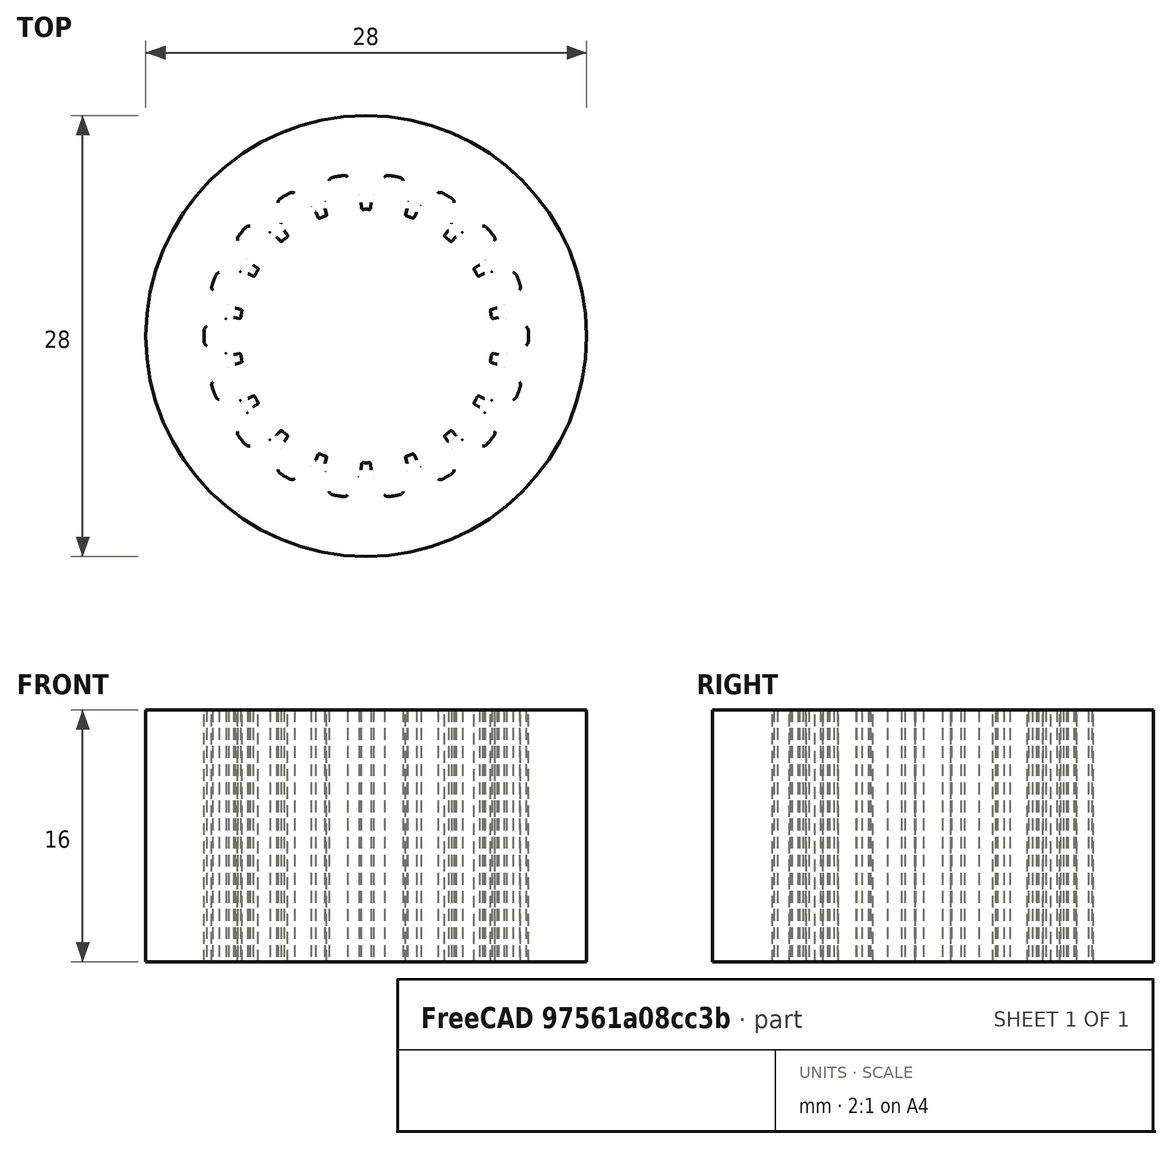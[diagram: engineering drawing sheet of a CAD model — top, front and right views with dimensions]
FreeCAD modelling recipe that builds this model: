
FCSTD DOCUMENT  (FreeCAD 0.19R24276 (Git))
Label: Gear_privod_perehodnik_to_GT2_gear_part_offset_3_d28_h16
License: All rights reserved
LicenseURL: http://en.wikipedia.org/wiki/All_rights_reserved
objects: Part::Part2DObjectPython×1, Part::Offset2D×1, Part::Cylinder×1, Part::Extrusion×1, Part::Cut×1
note: 5 computed .brp shape members not serialized (recipe doc carries the construction recipe); baked Part::Feature solids carry a one-line shape summary decoded from their .brp

FEATURE [Part::Part2DObjectPython] InvoluteGear  # Draft 2D object (typed FeaturePython)
  ExternalGear = true
  HighPrecision = true
  Modules = 1
  NumberOfTeeth = 18
  PressureAngle = 20
FEATURE [Part::Offset2D] Offset2D
  Fill = false
  Intersection = false
  Join = 0
  Mode = 1
  SelfIntersection = false
  Source = -> InvoluteGear
  Value = 0.3
FEATURE [Part::Cylinder] Cylinder  label="Цилиндр"
  Angle = 360
  AttacherType = Attacher::AttachEngine3D
  Height = 16
  Placement = pos=(0,0,-16) rot=(0,0,1;0rad)
  Radius = 14
FEATURE [Part::Extrusion] Extrude
  Base = -> Offset2D
  Dir = (0,0,-1)
  DirMode = 2
  FaceMakerClass = Part::FaceMakerBullseye
  LengthFwd = 16
  LengthRev = 0
  Solid = true
  Symmetric = false
FEATURE [Part::Cut] Cut
  Base = -> Cylinder
  Tool = -> Extrude
